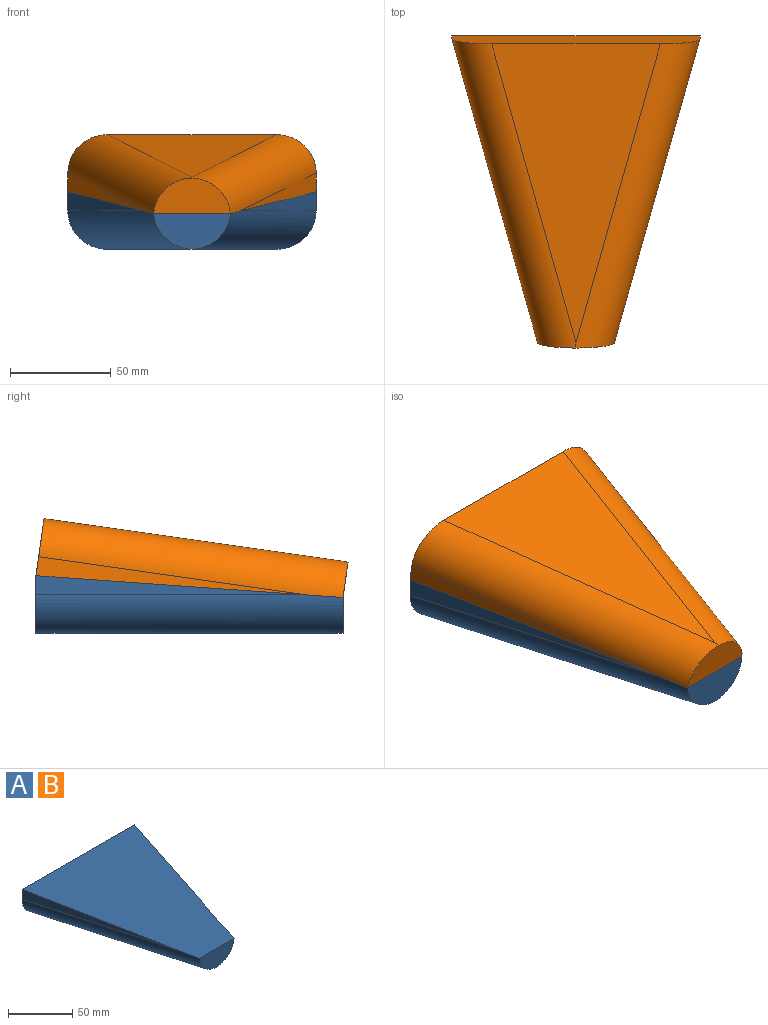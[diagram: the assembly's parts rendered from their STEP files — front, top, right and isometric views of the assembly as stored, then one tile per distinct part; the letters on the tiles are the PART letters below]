
ASSEMBLY  parts=2 mates=1
PART A: 8 faces, bbox 123.2x162.5x28.6 mm
  f0: plane 38.01x17.77mm, normal (0,-1,0), area 515.7mm2, adj f5,f6,f7
  f1: plane 134.47x37.54mm, normal (0.96,-0.27,0), area 664.9mm2, adj f2,f5,f6
  f2: plane 123.19x28.58mm, normal (0,1,0), area 3358.4mm2, adj f1,f3,f4,f5,f6,f7
  f3: plane 134.47x37.54mm, normal (-0.96,-0.27,0), area 664.9mm2, adj f2,f5,f7
  f4: plane 149.79x83.63mm, normal (0,0,-1), area 6263.7mm2, adj f2,f6,f7
  f5: plane 152.4x123.19mm, normal (0,-0.07,1), area 12320.6mm2, adj f0,f1,f2,f3,f6,f7
  f6: cylinder r=19.05mm len=162.46mm, axis (0.27,0.96,0), area 4722mm2, adj f0,f1,f2,f4,f5,f7
  f7: cylinder r=19.05mm len=162.46mm, axis (0.27,-0.96,0), area 4722mm2, adj f0,f2,f3,f4,f5,f6
PART B: same geometry as A
PLACE A t=(63.11,84.85,-55.97)mm
PLACE B rot(axis=(0,-1,-0.07),180deg) t=(63.11,80.82,0.9)mm
MATE fastened B.f5 <-> A.f5  axis (0,0.07,-1) through (63.11,84.85,-27.39)mm
